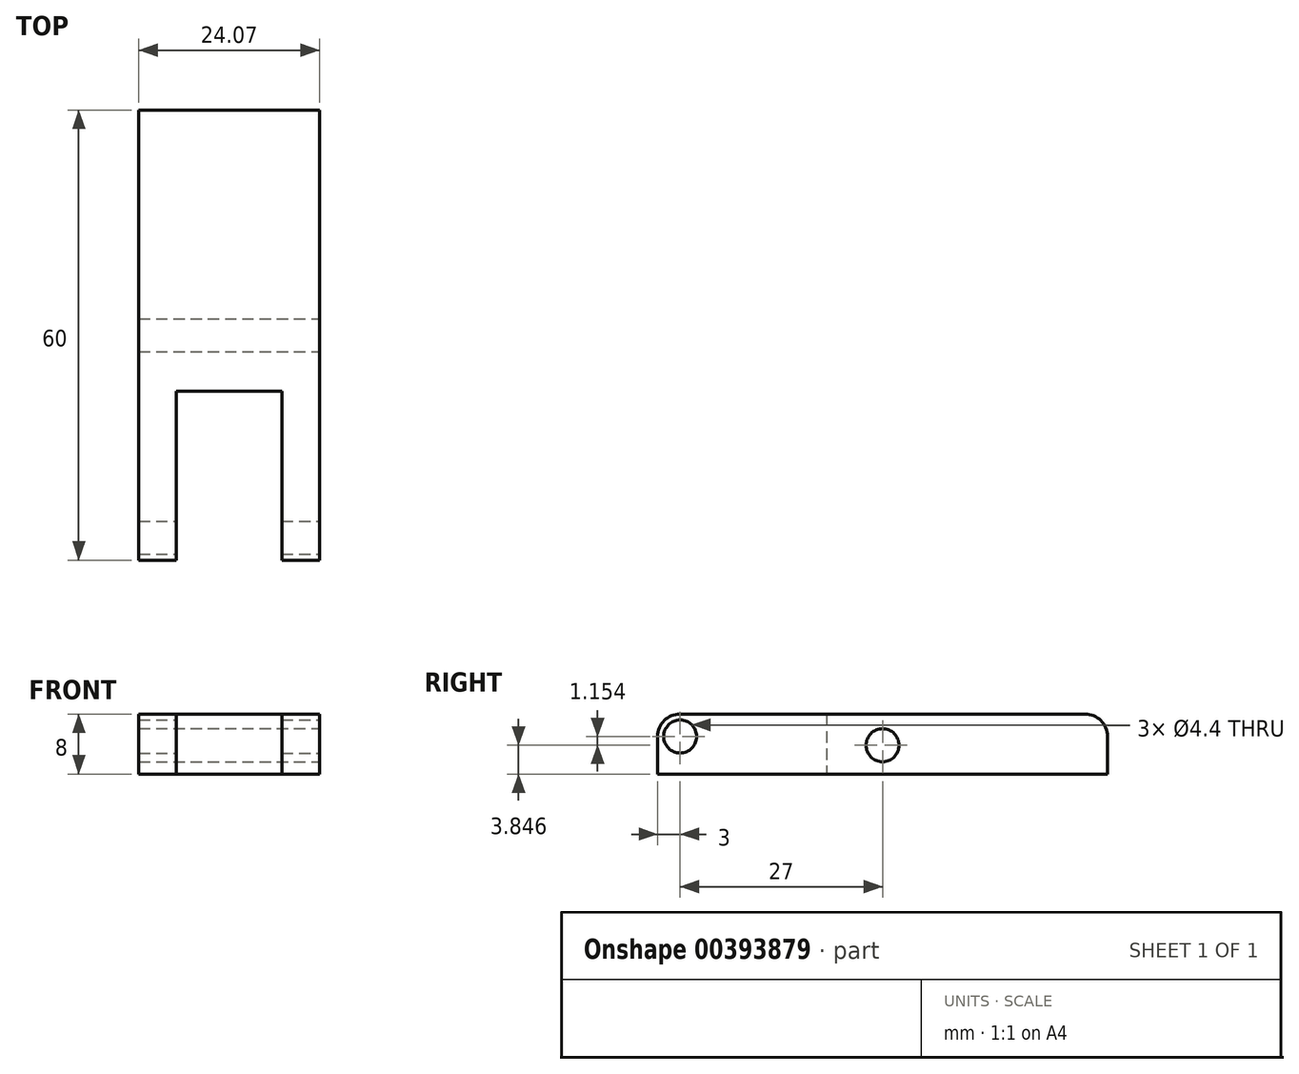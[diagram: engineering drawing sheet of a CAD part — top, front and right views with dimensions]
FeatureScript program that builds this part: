
annotation { "Feature Type Name" : "Feature", "Feature Type Description" : "" }
export const myFeature = defineFeature(function(context is Context, id is Id, definition is map)
    precondition{}
    {
        {
            var Q0;
            Q0=qCreatedBy(makeId("Top.planeOp"),FACE);
            var sketch = newSketch(context, id + "F0", { "sketchPlane" : qUnion([Q0])});
            skLineSegment(sketch, "E0", {"start": v(0, 0) * mm, "end": v(0, -30) * mm});
            skLineSegment(sketch, "E1", {"start": v(0, -30) * mm, "end": v(5, -30) * mm});
            skLineSegment(sketch, "E2", {"start": v(5, -30) * mm, "end": v(5, -7.45) * mm});
            skLineSegment(sketch, "E3", {"start": v(5, -7.45) * mm, "end": v(19.07, -7.45) * mm});
            skLineSegment(sketch, "E4", {"start": v(19.07, -7.45) * mm, "end": v(19.07, -30) * mm});
            skLineSegment(sketch, "E5", {"start": v(19.07, -30) * mm, "end": v(24.07, -30) * mm});
            skLineSegment(sketch, "E6", {"start": v(24.07, -30) * mm, "end": v(24.07, 30) * mm});
            skLineSegment(sketch, "E7", {"start": v(24.07, 30) * mm, "end": v(0, 30) * mm});
            skLineSegment(sketch, "E8", {"start": v(0, 30) * mm, "end": v(0, 0) * mm});
            skSolve(sketch);
        }
        {
            var Q0;
            Q0=makeQuery(id+"F0.imprint","IMPRINT",FACE,{"disambiguationData":[TD([[makeQuery(id+"F0.imprint","IMPRINT",EDGE,{"derivedFrom":sQuery(id+"F0.wireOp",EDGE,"E0")}),1.0]])]});
            extrude(context, id + "F1", {"entities" : qUnion([Q0]), "depth" : 8 * mm});
        }
        {
            var Q0;
            Q0=makeQuery(id+"F1.opExtrude","CAP_EDGE",EDGE,{"disambiguationData":[OSD([sQuery(id+"F0.wireOp",EDGE,"E5")])],"isStart":false});
            var Q1;
            Q1=makeQuery(id+"F1.opExtrude","CAP_EDGE",EDGE,{"disambiguationData":[OSD([sQuery(id+"F0.wireOp",EDGE,"E1")])],"isStart":false});
            var Q2;
            Q2=makeQuery(id+"F1.opExtrude","CAP_EDGE",EDGE,{"disambiguationData":[OSD([sQuery(id+"F0.wireOp",EDGE,"E7")])],"isStart":false});
            fillet(context, id + "F2", {"entities" : qUnion([Q0, Q1, Q2]), "radius" : 3 * mm, "tangentPropagation" : true, "allowEdgeOverflow" : false});
        }
        {
            var Q0;
            Q0=makeQuery(id+"F1.opExtrude","SWEPT_FACE",FACE,{"disambiguationData":[OSD([sQuery(id+"F0.wireOp",EDGE,"E6")])]});
            var sketch = newSketch(context, id + "F3", { "sketchPlane" : qUnion([Q0])});
            skPoint(sketch, "E9", {"position": v(-27, 5) * mm});
            skSolve(sketch);
        }
        {
            var Q0;
            Q0=sQuery(id+"F3.wireOp",VERTEX,"E9");
            var Q1;
            Q1=makeQuery(id+"F1.opExtrude","SWEPT_BODY",BODY,{"disambiguationData":[OSD([sQuery(id+"F0.wireOp",EDGE,"E0"),sQuery(id+"F0.wireOp",EDGE,"E1"),sQuery(id+"F0.wireOp",EDGE,"E2"),sQuery(id+"F0.wireOp",EDGE,"E3"),sQuery(id+"F0.wireOp",EDGE,"E4"),sQuery(id+"F0.wireOp",EDGE,"E5"),sQuery(id+"F0.wireOp",EDGE,"E6"),sQuery(id+"F0.wireOp",EDGE,"E7"),sQuery(id+"F0.wireOp",EDGE,"E8")])]});
            hole(context, id + "F4", {"style" : HoleStyle.SIMPLE, "endStyle" : HoleEndStyle.THROUGH, "standardTappedOrClearance" : lookupTablePath({ "standard" : "ISO", "fit" : "Normal", "size" : "M4", "type" : "Clearance" }), "standardBlindInLast" : lookupTablePath({ "fit" : "Standard", "standard" : "ISO", "size" : "M4", "type" : "Clearance" }), "holeDiameter" : 4.4 * mm, "isTappedThrough" : true, "tappedDepth" : 12 * mm, "tapClearance" : 3, "locations" : qUnion([Q0]), "scope" : qUnion([Q1])});
        }
        {
            var Q0;
            Q0=makeQuery(id+"F1.opExtrude","SWEPT_FACE",FACE,{"disambiguationData":[OSD([sQuery(id+"F0.wireOp",EDGE,"E6")])]});
            var sketch = newSketch(context, id + "F5", { "sketchPlane" : qUnion([Q0])});
            skPoint(sketch, "E10", {"position": v(0, 3.85) * mm});
            skSolve(sketch);
        }
        {
            var Q0;
            Q0=sQuery(id+"F5.wireOp",VERTEX,"E10");
            var Q1;
            Q1=makeQuery(id+"F1.opExtrude","SWEPT_BODY",BODY,{"disambiguationData":[OSD([sQuery(id+"F0.wireOp",EDGE,"E0"),sQuery(id+"F0.wireOp",EDGE,"E1"),sQuery(id+"F0.wireOp",EDGE,"E2"),sQuery(id+"F0.wireOp",EDGE,"E3"),sQuery(id+"F0.wireOp",EDGE,"E4"),sQuery(id+"F0.wireOp",EDGE,"E5"),sQuery(id+"F0.wireOp",EDGE,"E6"),sQuery(id+"F0.wireOp",EDGE,"E7"),sQuery(id+"F0.wireOp",EDGE,"E8")])]});
            hole(context, id + "F6", {"style" : HoleStyle.SIMPLE, "endStyle" : HoleEndStyle.THROUGH, "standardTappedOrClearance" : lookupTablePath({ "standard" : "ISO", "fit" : "Normal", "size" : "M4", "type" : "Clearance" }), "standardBlindInLast" : lookupTablePath({ "fit" : "Standard", "standard" : "ISO", "size" : "M4", "type" : "Clearance" }), "holeDiameter" : 4.4 * mm, "isTappedThrough" : true, "tappedDepth" : 12 * mm, "tapClearance" : 3, "locations" : qUnion([Q0]), "scope" : qUnion([Q1])});
        }
    });
